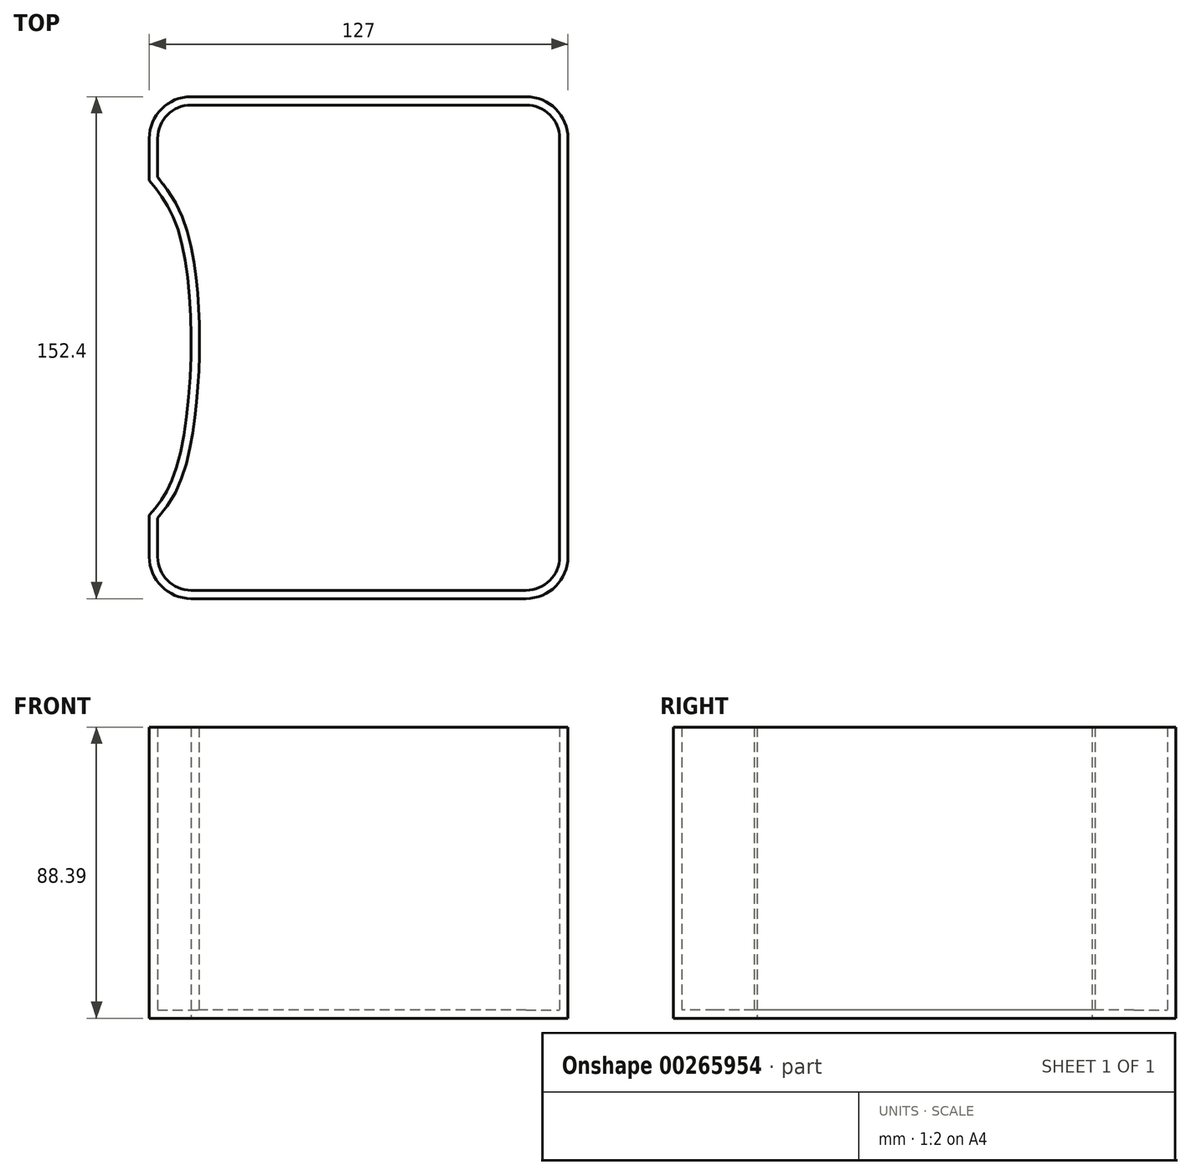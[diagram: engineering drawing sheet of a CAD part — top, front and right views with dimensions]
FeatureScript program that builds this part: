
annotation { "Feature Type Name" : "Feature", "Feature Type Description" : "" }
export const myFeature = defineFeature(function(context is Context, id is Id, definition is map)
    precondition{}
    {
        {
            var Q0;
            Q0=qCreatedBy(makeId("Top.planeOp"),FACE);
            var sketch = newSketch(context, id + "F0", { "sketchPlane" : qUnion([Q0])});
            skLineSegment(sketch, "E0.bottom", {"start": v(50.8, 76.2) * mm, "end": v(-50.8, 76.2) * mm});
            skLineSegment(sketch, "E0.top", {"start": v(50.8, -76.2) * mm, "end": v(-50.8, -76.2) * mm});
            skLineSegment(sketch, "E0.left", {"start": v(63.5, 63.5) * mm, "end": v(63.5, -63.5) * mm});
            skLineSegment(sketch, "E0.right", {"start": v(-63.5, 63.5) * mm, "end": v(-63.5, -63.5) * mm});
            skPoint(sketch, "E0.middle", {"position": v(0, 0) * mm});
            skPoint(sketch, "E1.visualSharp", {"position": v(-63.5, 76.2) * mm});
            skArc(sketch, "E1.filletArc", {"start": v(-50.8, 76.2) * mm, "mid": v(-59.78, 72.48) * mm, "end": v(-63.5, 63.5) * mm});
            skPoint(sketch, "E2.visualSharp", {"position": v(63.5, 76.2) * mm});
            skArc(sketch, "E2.filletArc", {"start": v(63.5, 63.5) * mm, "mid": v(59.78, 72.48) * mm, "end": v(50.8, 76.2) * mm});
            skPoint(sketch, "E3.visualSharp", {"position": v(63.5, -76.2) * mm});
            skArc(sketch, "E3.filletArc", {"start": v(50.8, -76.2) * mm, "mid": v(59.78, -72.48) * mm, "end": v(63.5, -63.5) * mm});
            skPoint(sketch, "E4.visualSharp", {"position": v(-63.5, -76.2) * mm});
            skArc(sketch, "E4.filletArc", {"start": v(-63.5, -63.5) * mm, "mid": v(-59.78, -72.48) * mm, "end": v(-50.8, -76.2) * mm});
            skLineSegment(sketch, "E5", {"start": v(-63.5, 50.8) * mm, "end": v(63.5, 50.8) * mm, "construction": true});
            skLineSegment(sketch, "E6", {"start": v(-63.5, -50.8) * mm, "end": v(63.5, -50.8) * mm, "construction": true});
            skLineSegment(sketch, "E7", {"start": v(50.8, 76.2) * mm, "end": v(50.8, -76.2) * mm, "construction": true});
            skLineSegment(sketch, "E8", {"start": v(-50.8, 76.2) * mm, "end": v(-50.8, -76.2) * mm, "construction": true});
            skFitSpline(sketch, "E9", {"points": [v(-63.5, 50.8) * mm, v(-55.58, 37.99) * mm, v(-50.8, 0) * mm, v(-56.44, -39.82) * mm, v(-63.5, -50.8) * mm], "startDerivative": vector(44.7, -55.48) * mm, "endDerivative": vector(-41.97, -48.74) * mm});
            skSolve(sketch);
        }
        {
            var Q0;
            Q0=makeQuery(id+"F0.imprint","IMPRINT",FACE,{"disambiguationData":[TD([[makeQuery(id+"F0.imprint","IMPRINT",EDGE,{"derivedFrom":sQuery(id+"F0.wireOp",EDGE,"E0.bottom")}),1.0]])]});
            extrude(context, id + "F1", {"entities" : qUnion([Q0]), "depth" : 88.4 * mm});
        }
        {
            var Q0;
            Q0=makeQuery(id+"F1.opExtrude","CAP_FACE",FACE,{"disambiguationData":[OSD([sQuery(id+"F0.wireOp",EDGE,"E0.bottom"),sQuery(id+"F0.wireOp",EDGE,"E0.top"),sQuery(id+"F0.wireOp",EDGE,"E0.left"),sQuery(id+"F0.wireOp",EDGE,"E0.right"),sQuery(id+"F0.wireOp",EDGE,"E1.filletArc"),sQuery(id+"F0.wireOp",EDGE,"E2.filletArc"),sQuery(id+"F0.wireOp",EDGE,"E3.filletArc"),sQuery(id+"F0.wireOp",EDGE,"E4.filletArc"),sQuery(id+"F0.wireOp",EDGE,"E9")])],"isStart":false});
            shell(context, id + "F2", {"entities" : qUnion([Q0]), "thickness" : 2.54 * mm});
        }
    });
